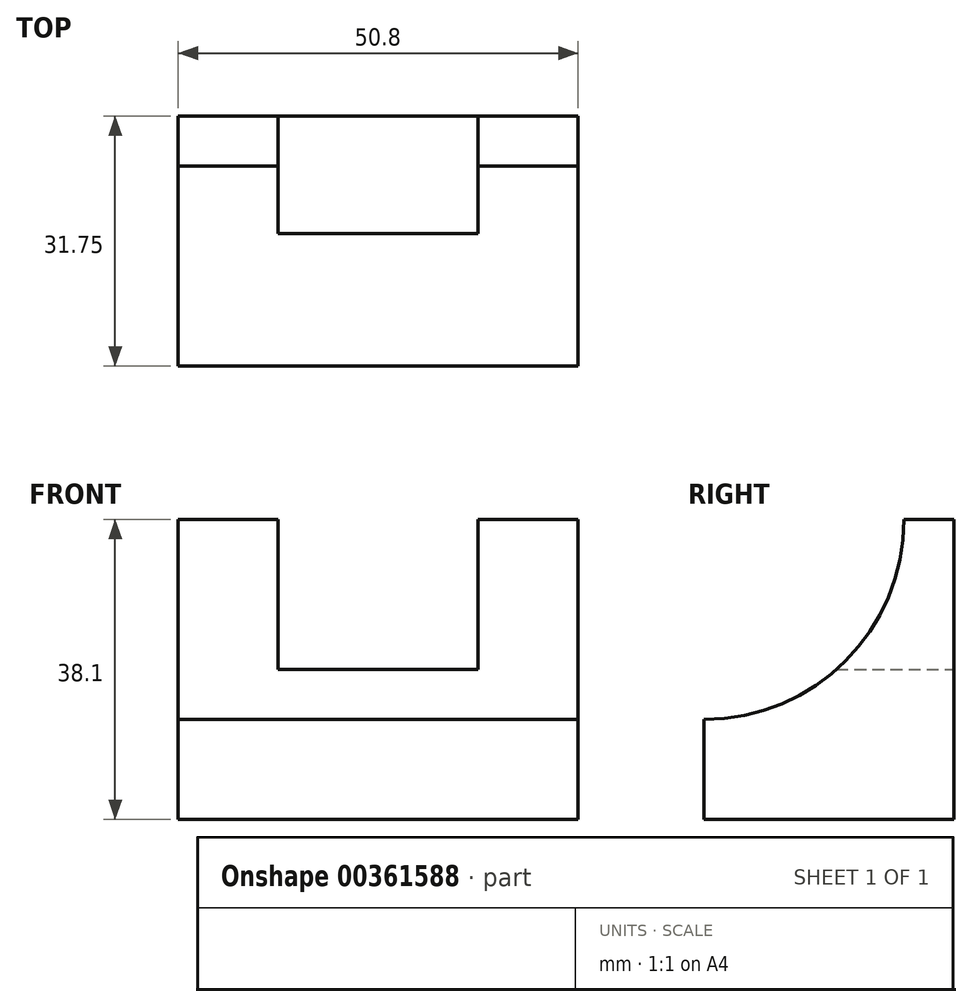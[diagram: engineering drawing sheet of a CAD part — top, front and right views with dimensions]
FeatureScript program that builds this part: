
annotation { "Feature Type Name" : "Feature", "Feature Type Description" : "" }
export const myFeature = defineFeature(function(context is Context, id is Id, definition is map)
    precondition{}
    {
        {
            var Q0;
            Q0=qCreatedBy(makeId("Front.planeOp"),FACE);
            var sketch = newSketch(context, id + "F0", { "sketchPlane" : qUnion([Q0])});
            skLineSegment(sketch, "E0", {"start": v(0, 0) * mm, "end": v(50.8, 0) * mm});
            skLineSegment(sketch, "E1", {"start": v(50.8, 0) * mm, "end": v(50.8, 38.1) * mm});
            skLineSegment(sketch, "E2", {"start": v(50.8, 38.1) * mm, "end": v(0, 38.1) * mm});
            skLineSegment(sketch, "E3", {"start": v(0, 38.1) * mm, "end": v(0, 0) * mm});
            skSolve(sketch);
        }
        {
            var Q0;
            Q0=makeQuery(id+"F0.imprint","IMPRINT",FACE,{"disambiguationData":[TD([[makeQuery(id+"F0.imprint","IMPRINT",EDGE,{"derivedFrom":sQuery(id+"F0.wireOp",EDGE,"E0")}),1.0]])]});
            extrude(context, id + "F1", {"entities" : qUnion([Q0]), "depth" : 31.75 * mm});
        }
        {
            var Q0;
            Q0=makeQuery(id+"F1.opExtrude","SWEPT_FACE",FACE,{"disambiguationData":[OSD([sQuery(id+"F0.wireOp",EDGE,"E1")])]});
            var sketch = newSketch(context, id + "F2", { "sketchPlane" : qUnion([Q0])});
            skCircle(sketch, "E4", {"center": v(-31.75, 38.1) * mm, "radius": 25.4 * mm});
            skSolve(sketch);
        }
        {
            var Q0;
            {var subQ0=sQuery(id+"F2.wireOp",EDGE,"E4");var subQ1=sQuery(id+"F0.wireOp",EDGE,"E1");var subQ4=makeQuery(id+"F1.opExtrude","CAP_EDGE",EDGE,{"disambiguationData":[OSD([subQ1])],"isStart":false});var subQ5=makeQuery(id+"F2.imprint","INTERSECT",VERTEX,{"derivedFrom":[subQ4,subQ0]});Q0=makeQuery(id+"F2.imprint","IMPRINT",FACE,{"disambiguationData":[TD([[makeQuery(id+"F2.imprint","IMPRINT",EDGE,{"disambiguationData":[TD([[subQ5,1.0]])],"derivedFrom":subQ0}),1.0]])]});}
            var Q1;
            {var subQ0=sQuery(id+"F2.wireOp",EDGE,"E4");var subQ1=sQuery(id+"F0.wireOp",EDGE,"E1");var subQ4=makeQuery(id+"F1.opExtrude","CAP_EDGE",EDGE,{"disambiguationData":[OSD([subQ1])],"isStart":false});var subQ5=makeQuery(id+"F2.imprint","INTERSECT",VERTEX,{"derivedFrom":[subQ4,subQ0]});Q1=makeQuery(id+"F2.imprint","IMPRINT",FACE,{"disambiguationData":[TD([[makeQuery(id+"F2.imprint","IMPRINT",EDGE,{"disambiguationData":[TD([[subQ5,-1.0]])],"derivedFrom":subQ0}),1.0]])]});}
            extrude(context, id + "F3", {"entities" : qUnion([Q0, Q1]), "operationType" : NewBodyOperationType.REMOVE, "oppositeDirection" : true, "depth" : 50.8 * mm});
        }
        {
            var Q0;
            Q0=makeQuery(id+"F1.opExtrude","CAP_FACE",FACE,{"disambiguationData":[OSD([sQuery(id+"F0.wireOp",EDGE,"E0"),sQuery(id+"F0.wireOp",EDGE,"E1"),sQuery(id+"F0.wireOp",EDGE,"E2"),sQuery(id+"F0.wireOp",EDGE,"E3")])],"isStart":true});
            var sketch = newSketch(context, id + "F4", { "sketchPlane" : qUnion([Q0])});
            skLineSegment(sketch, "E5", {"start": v(-38.1, 38.1) * mm, "end": v(-38.1, 19.05) * mm});
            skLineSegment(sketch, "E6", {"start": v(-38.1, 19.05) * mm, "end": v(-12.7, 19.05) * mm});
            skLineSegment(sketch, "E7", {"start": v(-12.7, 19.05) * mm, "end": v(-12.7, 38.1) * mm});
            skSolve(sketch);
        }
        {
            var Q0;
            {var subQ0=sQuery(id+"F4.wireOp",EDGE,"E5");Q0=makeQuery(id+"F4.imprint","IMPRINT",FACE,{"disambiguationData":[TD([[makeQuery(id+"F4.imprint","IMPRINT",EDGE,{"derivedFrom":subQ0}),1.0]])]});}
            extrude(context, id + "F5", {"entities" : qUnion([Q0]), "operationType" : NewBodyOperationType.REMOVE, "oppositeDirection" : true, "depth" : 19.05 * mm});
        }
    });
